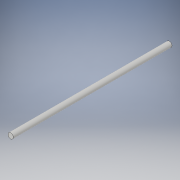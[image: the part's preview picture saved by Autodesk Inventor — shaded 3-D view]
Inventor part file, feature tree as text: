
AUTODESK INVENTOR PART (.ipt)
format: ipt  version: 2017 (Build 210142000, 142)  size: 94,208 bytes
history: native  units: in
note: dims shown in document units (in); Inventor stores cm internally (conversion verified against a paired STEP export)
features: extrude x2, sketch x2
ambient origin geometry x8: Origin, YZ Plane, XZ Plane, XY Plane, X Axis, Y Axis, Z Axis, Center Point
bodies: Solid1 (feature_tree)
feature tree (4):
  extrude  "Extrusion1"  Depth=11.75in TaperAngle=0.0deg
  extrude  "Extrusion2"  [1 undecoded]
  sketch  "Sketch1"  dims[d0=0.4in d1=11.75in d2=0.0in]
  sketch  "Sketch2"  dims[d3=0.125in d4=0.0in]
note: 1 required parameter value undecoded (feature->parameter linkage not recoverable at this tier; creation-order binding heuristic only, values carry confidence <= 0.55)
